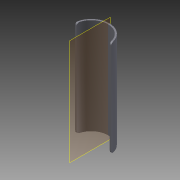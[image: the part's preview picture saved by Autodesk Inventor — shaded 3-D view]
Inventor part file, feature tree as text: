
AUTODESK INVENTOR PART (.ipt)
format: ipt  version: 2015 (Build 190159000, 159)  size: 87,552 bytes
history: native  units: mm
features: extrude x1, fillet x1
ambient origin geometry x8: Origin, YZ Plane, XZ Plane, XY Plane, X Axis, Y Axis, Z Axis, Center Point
bodies: Solid1 (feature_tree)
feature tree (2):
  extrude  "Extrusión1"  Depth=37.0mm
  fillet  "Empalme1"  Radius=1.5mm
